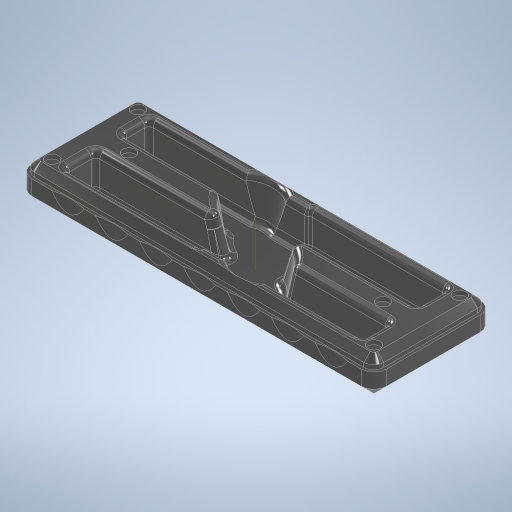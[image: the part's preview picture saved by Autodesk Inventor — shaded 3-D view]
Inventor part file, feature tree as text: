
AUTODESK INVENTOR PART (.ipt)
format: ipt  version: 2024.1 (Build 281209000, 209)  size: 2,156,032 bytes
history: native  units: mm
features: projected_geometry x29, extrude x20, fillet x11, chamfer x5, other x4, pattern_circular x2, sketch x2, plane x1, pattern_linear x1, mirror x1
ambient origin geometry x8: Origin, YZ Plane, XZ Plane, XY Plane, X Axis, Y Axis, Z Axis, Center Point
bodies: Body1 (feature_tree), Body2 (feature_tree), Body3 (feature_tree)
feature tree (76):
  other  "case"
  extrude  "Extrusion1"  Depth=56.0mm
  extrude  "Extrusion2"  Depth=28.0mm
  extrude  "Extrusion3"  Depth=18.0mm TaperAngle=0.0deg
  fillet  "Fillet1"  Radius=2.0mm
  fillet  "Fillet2"  Radius=4.0mm
  fillet  "Fillet3"  Radius=20.0mm
  pattern_circular  "Circular Pattern1"  [2 undecoded]
  fillet  "Fillet4"  Radius=20.0mm
  chamfer  "Chamfer1"  Distance=96.0mm
  extrude  "Extrusion4"  Depth=65.0mm
  chamfer  "Chamfer2"  Distance=74.2mm
  extrude  "Extrusion5"  Depth=12.0mm
  pattern_circular  "Circular Pattern2"  [2 undecoded]
  fillet  "Fillet5"  Radius=12.4mm
  fillet  "Fillet6"  Radius=0.95mm
  fillet  "Fillet10"  Radius=0.95mm
  fillet  "Fillet11"  Radius=2.0mm
  fillet  "Fillet12"  Radius=3.7mm
  extrude  "Extrusion6"  Depth=17.6mm TaperAngle=0.0deg
  plane  "Work Plane1"
  extrude  "Extrusion7"  Depth=25.0mm
  extrude  "Extrusion8"  Depth=16.6mm
  extrude  "Extrusion9"  Depth=4.0mm
  fillet  "Fillet8"  Radius=3.0mm
  extrude  "Extrusion10"  Depth=4.0mm
  pattern_linear  "Rectangular Pattern1"  Count1=2 Spacing1=180.0deg
  mirror  "Mirror1"
  extrude  "Extrusion11"  Depth=6.0mm
  extrude  "Extrusion15"  Depth=6.0mm TaperAngle=45.0deg
  extrude  "Extrusion16"  Depth=1.3mm
  chamfer  "Chamfer4"  Distance=5.0mm
  extrude  "Extrusion18"  Depth=3.0mm TaperAngle=45.0deg
  extrude  "Extrusion19"  Depth=6.0mm
  extrude  "Extrusion12"  Depth=6.5mm
  extrude  "Extrusion13"  Depth=6.5mm
  extrude  "Extrusion14"  Depth=22.0mm
  extrude  "Extrusion17"  Depth=2.0mm TaperAngle=0.0deg
  chamfer  "Chamfer5"  Distance=20.0mm Angle=360.0deg
  chamfer  "Chamfer6"  Distance=6.5mm
  extrude  "Extrusion20"  Depth=6.5mm
  fillet  "Fillet13"  Radius=2.0mm
  projected_geometry  "Projected Loop1"
  projected_geometry  "Projected Loop5"
  other  "Work Axis1"
  projected_geometry  "Projected Loop7"
  other  "lid"
  projected_geometry  "Projected Loop8"
  projected_geometry  "Projected Loop9"
  projected_geometry  "Projected Loop10"
  projected_geometry  "Projected Loop11"
  sketch  "Sketch15"  dims[d0=167.0mm d1=56.0mm]
  sketch  "Sketch16"  dims[d2=83.5mm d3=28.0mm d4=18.0mm d5=0.0mm d6=2.0mm d8=4.0mm d9=20.0mm d10=4.0mm d11=20.0mm d12=96.0mm d13=65.0mm d14=74.2mm d15=12.0mm d16=14.3mm d17=12.4mm d18=0.95mm d19=0.95mm d20=2.0mm d21=3.7mm d22=17.6mm d23=0.0mm d24=25.0mm d27=16.6mm d28=-1.745329mm d29=4.0mm d30=3.0mm d31=4.0mm d32=20.0mm d33=180.0deg d35=6.0mm d36=6.0mm d37=2.0mm d38=45.0deg d39=1.3mm d40=5.0mm d41=0.0mm d42=3.0mm d43=2.0mm d44=45.0deg d45=6.0mm d46=6.5mm d47=6.5mm d48=22.0mm d49=2.0mm d50=0.0mm d51=20.0mm d52=360.0deg d54=6.5mm d55=6.5mm d56=2.0mm d57=3.0mm d59=6.5mm d60=6.45mm d61=1.0mm d62=3.0mm d63=0.0mm d64=3.1mm d65=0.0mm d69=1.8mm d70=0.0mm d71=0.5mm d72=1.0mm d73=0.0mm d74=0.5mm d75=60.0mm d76=20.0mm d77=29.0mm d79=8.5mm d80=-1.745329mm d82=70.0mm d84=124.0mm d85=55.0mm d86=1.0mm d89=0.06mm d90=0.0mm d91=0.02mm d92=0.0mm d93=30.0deg d94=1.0mm d95=6.0mm d96=6.0mm d97=7.0mm d98=6.0mm d99=6.0mm d101=1.0mm d108=3.0mm d109=3.0mm d110=0.04mm d111=0.0mm d112=1.6mm d113=1.6mm d114=1.1mm d115=1.1mm d116=7.0mm d117=3.0mm d119=2.0mm d120=1.1mm d121=1.1mm d122=1.5mm d123=1.5mm d124=1.5mm d125=1.0mm d126=1.1mm d127=1.1mm d128=1.8mm d131=2.0mm d132=1.5mm d133=1.5mm d140=50.0mm d142=8.0mm d143=60.0mm d145=8.0mm d148=0.0mm d149=0.0mm d150=0.0mm d151=0.0mm d152=3.5mm d153=0.0mm d154=2.5mm d155=2.0mm d156=45.0deg d158=0.4mm d159=0.4mm d160=0.0mm d163=3.0mm d164=1.5mm d165=0.4mm d166=0.0mm d167=3.1mm d168=0.0mm d169=1.5mm d170=2.0mm d171=45.0deg d172=1.5mm d173=2.0mm d174=45.0deg d175=8.0mm d176=8.0mm d177=45.0mm d178=16.0mm d179=3.0mm d180=3.0mm d181=3.0mm d182=0.0mm d183=0.0mm d184=1.0mm]
  other  "lid-part2"
  projected_geometry  "Projected Loop12"
  projected_geometry  "Projected Loop13"
  projected_geometry  "Projected Loop14"
  projected_geometry  "Projected Loop15"
  projected_geometry  "Projected Loop16"
  projected_geometry  "Projected Loop17"
  projected_geometry  "Projected Loop18"
  projected_geometry  "Projected Loop19"
  projected_geometry  "Projected Loop20"
  projected_geometry  "Projected Loop21"
  projected_geometry  "Projected Loop22"
  projected_geometry  "Projected Loop23"
  projected_geometry  "Projected Loop24"
  projected_geometry  "Projected Loop25"
  projected_geometry  "Projected Loop26"
  projected_geometry  "Projected Loop27"
  projected_geometry  "Projected Loop28"
  projected_geometry  "Projected Loop29"
  projected_geometry  "Projected Loop30"
  projected_geometry  "Projected Loop31"
  projected_geometry  "Projected Loop32"
  projected_geometry  "Projected Loop33"
note: 4 required parameter values undecoded (feature->parameter linkage not recoverable at this tier; creation-order binding heuristic only, values carry confidence <= 0.55)
